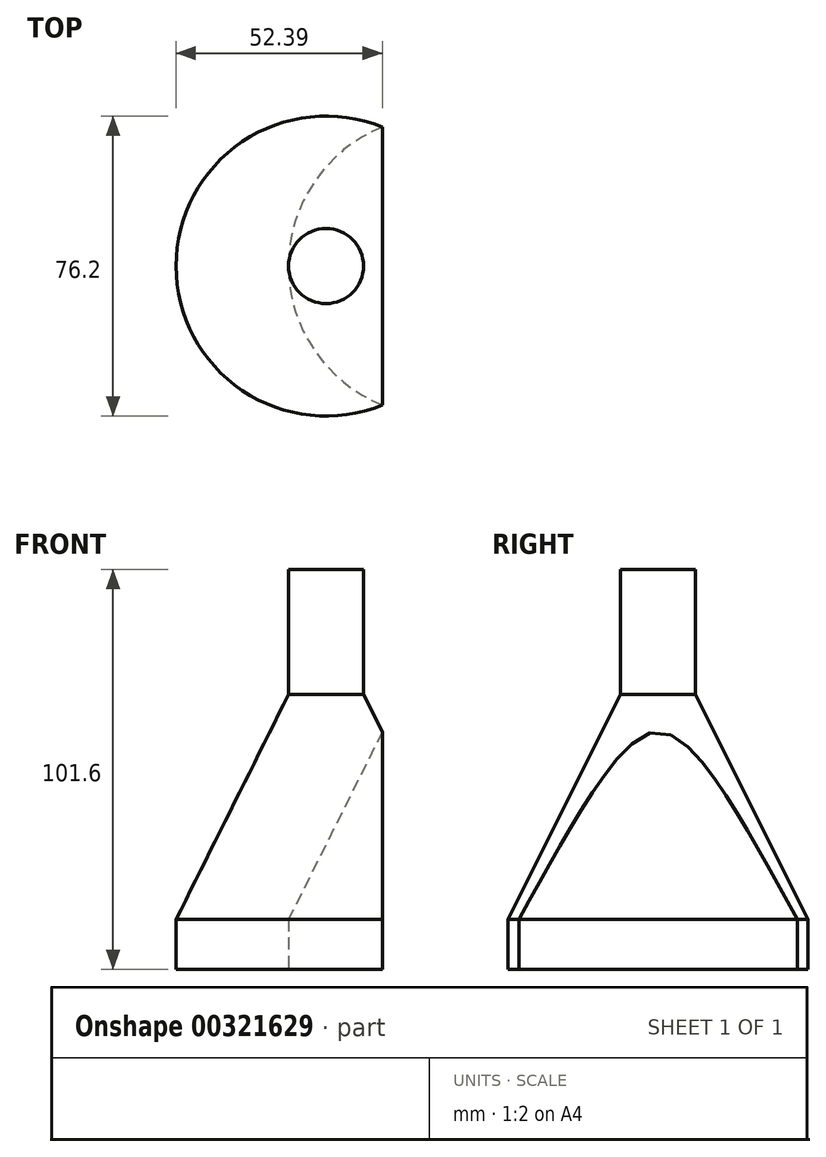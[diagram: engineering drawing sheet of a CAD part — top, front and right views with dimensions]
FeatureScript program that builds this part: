
annotation { "Feature Type Name" : "Feature", "Feature Type Description" : "" }
export const myFeature = defineFeature(function(context is Context, id is Id, definition is map)
    precondition{}
    {
        {
            var Q0;
            Q0=qCreatedBy(makeId("Front.planeOp"),FACE);
            var sketch = newSketch(context, id + "F0", { "sketchPlane" : qUnion([Q0])});
            skLineSegment(sketch, "E0", {"start": v(0, 0) * mm, "end": v(0, 31.75) * mm, "construction": true});
            skLineSegment(sketch, "E1", {"start": v(0, 31.75) * mm, "end": v(9.52, 31.75) * mm});
            skLineSegment(sketch, "E2", {"start": v(9.53, 31.75) * mm, "end": v(9.53, 0) * mm});
            skLineSegment(sketch, "E3", {"start": v(9.52, 0) * mm, "end": v(38.1, -57.15) * mm});
            skLineSegment(sketch, "E4", {"start": v(38.1, -57.15) * mm, "end": v(38.1, -69.85) * mm});
            skLineSegment(sketch, "E5", {"start": v(38.1, -69.85) * mm, "end": v(0, -69.85) * mm});
            skLineSegment(sketch, "E6", {"start": v(0, 31.75) * mm, "end": v(0, -69.85) * mm});
            skSolve(sketch);
        }
        {
            var Q0;
            Q0=qSketchRegion(id+"F0",true);
            var Q1;
            Q1=sQuery(id+"F0.wireOp",EDGE,"E0");
            revolve(context, id + "F1", {"entities" : qUnion([Q0]), "axis" : qUnion([Q1]), "revolveType" : RevolveType.FULL});
        }
        {
            var Q0;
            Q0=makeQuery(id+"F1.opRevolve","SWEPT_BODY",BODY,{"disambiguationData":[OSD([sQuery(id+"F0.wireOp",EDGE,"E1"),sQuery(id+"F0.wireOp",EDGE,"E2"),sQuery(id+"F0.wireOp",EDGE,"E3"),sQuery(id+"F0.wireOp",EDGE,"E4"),sQuery(id+"F0.wireOp",EDGE,"E5"),sQuery(id+"F0.wireOp",EDGE,"6cffce98-ed6d-4752-95ab-70827d12d298.0"),sQuery(id+"F0.wireOp",EDGE,"6cffce98-ed6d-4752-95ab-70827d12d298.1"),sQuery(id+"F0.wireOp",EDGE,"6cffce98-ed6d-4752-95ab-70827d12d298.2"),sQuery(id+"F0.wireOp",EDGE,"6cffce98-ed6d-4752-95ab-70827d12d298.3"),sQuery(id+"F0.wireOp",EDGE,"6cffce98-ed6d-4752-95ab-70827d12d298.4"),sQuery(id+"F0.wireOp",EDGE,"LZUBdMsW-NZLa-2cMp-E1xW-asSrOQVLWIoc"),sQuery(id+"F0.wireOp",EDGE,"LHPwzYbd-iZi3-Sxs4-8aeP-KWnq5UMweIE4")])]});
            transform(context, id + "F2", {"entities" : qUnion([Q0]), "transformType" : TransformType.TRANSLATION_3D, "dx" : 28.57 * mm, "dy" : 0 * mm, "dz" : 0 * mm, "makeCopy" : true});
        }
        {
            var Q0;
            Q0=makeQuery(id+"F2.opPattern","COPY",BODY,{"derivedFrom":makeQuery(id+"F1.opRevolve","SWEPT_BODY",BODY,{"disambiguationData":[OSD([sQuery(id+"F0.wireOp",EDGE,"E1"),sQuery(id+"F0.wireOp",EDGE,"E2"),sQuery(id+"F0.wireOp",EDGE,"E3"),sQuery(id+"F0.wireOp",EDGE,"E4"),sQuery(id+"F0.wireOp",EDGE,"E5"),sQuery(id+"F0.wireOp",EDGE,"6cffce98-ed6d-4752-95ab-70827d12d298.0"),sQuery(id+"F0.wireOp",EDGE,"6cffce98-ed6d-4752-95ab-70827d12d298.1"),sQuery(id+"F0.wireOp",EDGE,"6cffce98-ed6d-4752-95ab-70827d12d298.2"),sQuery(id+"F0.wireOp",EDGE,"6cffce98-ed6d-4752-95ab-70827d12d298.3"),sQuery(id+"F0.wireOp",EDGE,"6cffce98-ed6d-4752-95ab-70827d12d298.4"),sQuery(id+"F0.wireOp",EDGE,"LZUBdMsW-NZLa-2cMp-E1xW-asSrOQVLWIoc"),sQuery(id+"F0.wireOp",EDGE,"LHPwzYbd-iZi3-Sxs4-8aeP-KWnq5UMweIE4")])]}),"instanceName":"1"});
            var Q1;
            Q1=makeQuery(id+"F1.opRevolve","SWEPT_BODY",BODY,{"disambiguationData":[OSD([sQuery(id+"F0.wireOp",EDGE,"E1"),sQuery(id+"F0.wireOp",EDGE,"E2"),sQuery(id+"F0.wireOp",EDGE,"E3"),sQuery(id+"F0.wireOp",EDGE,"E4"),sQuery(id+"F0.wireOp",EDGE,"E5"),sQuery(id+"F0.wireOp",EDGE,"6cffce98-ed6d-4752-95ab-70827d12d298.0"),sQuery(id+"F0.wireOp",EDGE,"6cffce98-ed6d-4752-95ab-70827d12d298.1"),sQuery(id+"F0.wireOp",EDGE,"6cffce98-ed6d-4752-95ab-70827d12d298.2"),sQuery(id+"F0.wireOp",EDGE,"6cffce98-ed6d-4752-95ab-70827d12d298.3"),sQuery(id+"F0.wireOp",EDGE,"6cffce98-ed6d-4752-95ab-70827d12d298.4"),sQuery(id+"F0.wireOp",EDGE,"LZUBdMsW-NZLa-2cMp-E1xW-asSrOQVLWIoc"),sQuery(id+"F0.wireOp",EDGE,"LHPwzYbd-iZi3-Sxs4-8aeP-KWnq5UMweIE4")])]});
            booleanBodies(context, id + "F3", {"operationType" : BooleanOperationType.SUBTRACTION, "tools" : qUnion([Q0]), "targets" : qUnion([Q1])});
        }
    });
